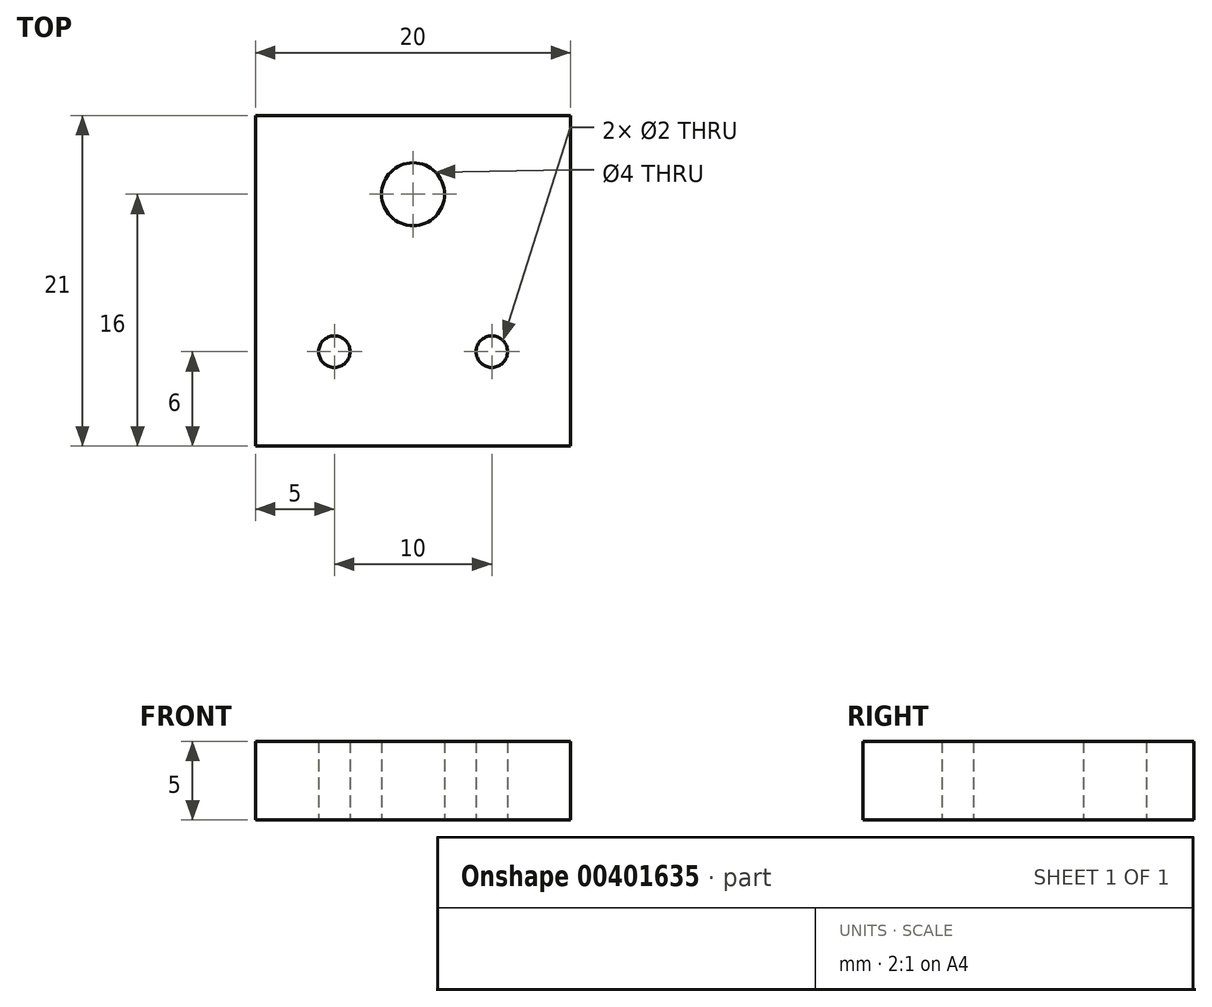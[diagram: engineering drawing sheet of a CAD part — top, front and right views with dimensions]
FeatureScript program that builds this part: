
annotation { "Feature Type Name" : "Feature", "Feature Type Description" : "" }
export const myFeature = defineFeature(function(context is Context, id is Id, definition is map)
    precondition{}
    {
        {
            var Q0;
            Q0=qCreatedBy(makeId("Top.planeOp"),FACE);
            var sketch = newSketch(context, id + "F0", { "sketchPlane" : qUnion([Q0])});
            skLineSegment(sketch, "E0.bottom", {"start": v(-10, 15) * mm, "end": v(10, 15) * mm});
            skLineSegment(sketch, "E0.top", {"start": v(-10, -6) * mm, "end": v(10, -6) * mm});
            skLineSegment(sketch, "E0.left", {"start": v(-10, 15) * mm, "end": v(-10, -6) * mm});
            skLineSegment(sketch, "E0.right", {"start": v(10, 15) * mm, "end": v(10, -6) * mm});
            skPoint(sketch, "E1", {"position": v(0, 15) * mm});
            skCircle(sketch, "E2", {"center": v(-5, 0) * mm, "radius": 1 * mm});
            skCircle(sketch, "E3", {"center": v(5, 0) * mm, "radius": 1 * mm});
            skCircle(sketch, "E4", {"center": v(0, 10) * mm, "radius": 2 * mm});
            skSolve(sketch);
        }
        {
            var Q0;
            Q0=makeQuery(id+"F0.imprint","IMPRINT",FACE,{"disambiguationData":[TD([[makeQuery(id+"F0.imprint","IMPRINT",EDGE,{"derivedFrom":sQuery(id+"F0.wireOp",EDGE,"E0.bottom")}),-1.0]])]});
            extrude(context, id + "F1", {"entities" : qUnion([Q0]), "depth" : 5 * mm});
        }
    });
